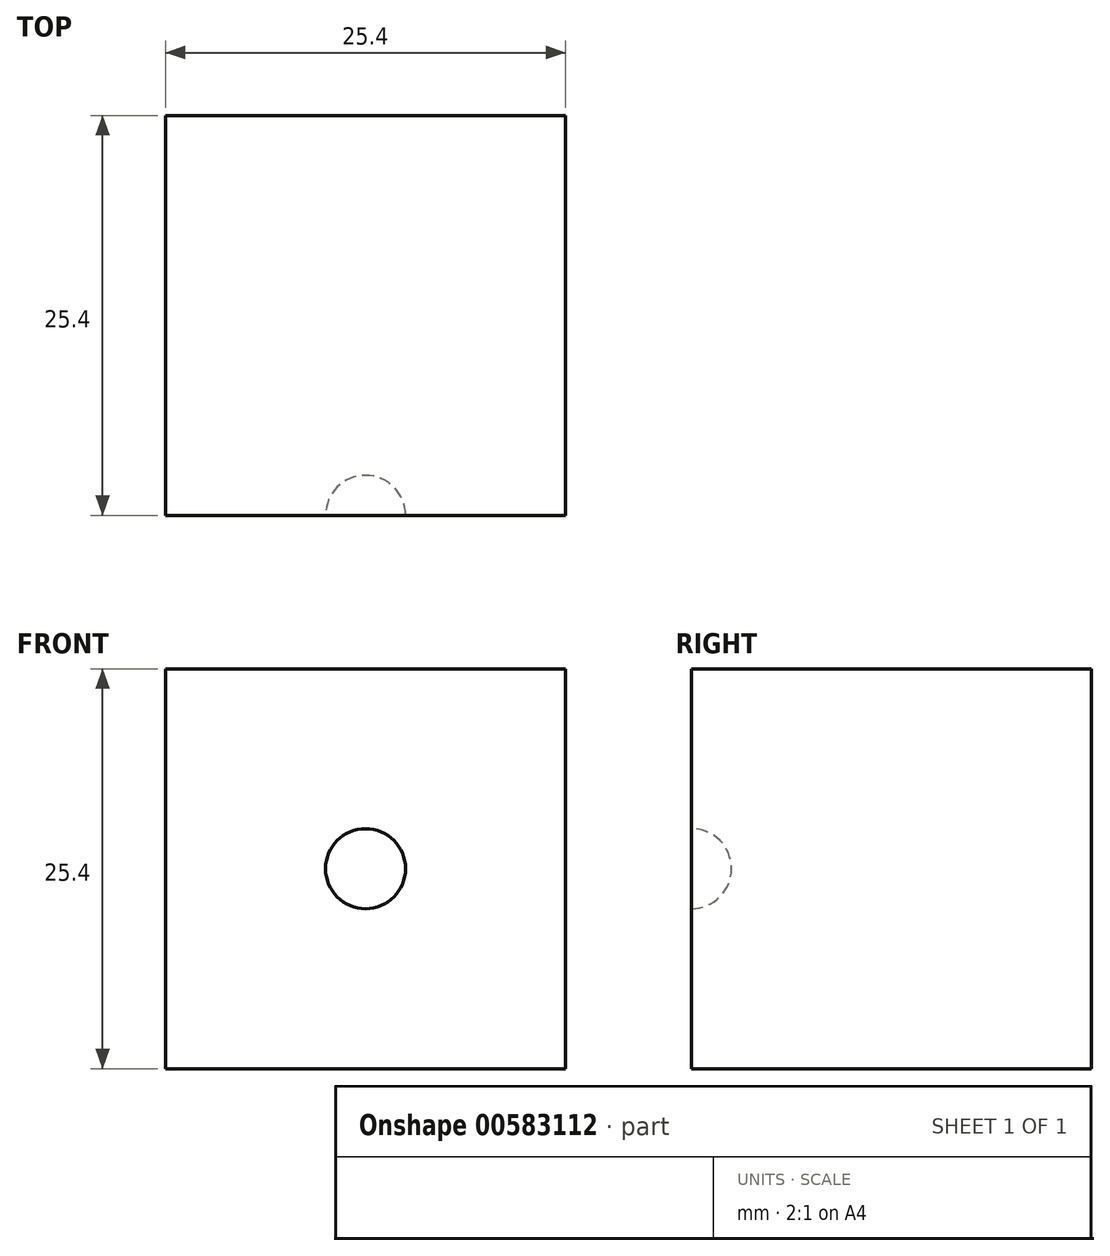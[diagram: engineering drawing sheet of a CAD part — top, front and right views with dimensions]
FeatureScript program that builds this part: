
annotation { "Feature Type Name" : "Feature", "Feature Type Description" : "" }
export const myFeature = defineFeature(function(context is Context, id is Id, definition is map)
    precondition{}
    {
        {
            var Q0;
            Q0=qCreatedBy(makeId("Front.planeOp"),FACE);
            var sketch = newSketch(context, id + "F0", { "sketchPlane" : qUnion([Q0])});
            skLineSegment(sketch, "E0.bottom", {"start": v(0, 0) * mm, "end": v(25.4, 0) * mm});
            skLineSegment(sketch, "E0.top", {"start": v(0, 25.4) * mm, "end": v(25.4, 25.4) * mm});
            skLineSegment(sketch, "E0.left", {"start": v(0, 0) * mm, "end": v(0, 25.4) * mm});
            skLineSegment(sketch, "E0.right", {"start": v(25.4, 0) * mm, "end": v(25.4, 25.4) * mm});
            skSolve(sketch);
        }
        {
            var Q0;
            Q0 = qSketchRegion(id + "F0", true);
            extrude(context, id + "F1", {"entities" : qUnion([Q0]), "depth" : 25.4 * mm, "offsetDistance" : 25.4 * mm});
        }
        {
            var Q0;
            Q0=makeQuery(id+"F1.opExtrude","CAP_FACE",FACE,{"disambiguationData":[OSD([sQuery(id+"F0.wireOp",EDGE,"E0.bottom"),sQuery(id+"F0.wireOp",EDGE,"E0.top"),sQuery(id+"F0.wireOp",EDGE,"E0.left"),sQuery(id+"F0.wireOp",EDGE,"E0.right")])],"isStart":false});
            var sketch = newSketch(context, id + "F2", { "sketchPlane" : qUnion([Q0])});
            skLineSegment(sketch, "E1", {"start": v(12.7, 25.4) * mm, "end": v(12.7, 0) * mm});
            skArc(sketch, "E2", {"start": v(12.7, 10.16) * mm, "mid": v(15.24, 12.7) * mm, "end": v(12.7, 15.24) * mm});
            skSolve(sketch);
        }
        {
            var Q0;
            Q0 = qSketchRegion(id + "F2", true);
            var Q1;
            Q1=sQuery(id+"F2.wireOp",EDGE,"E1");
            revolve(context, id + "F3", {"operationType" : NewBodyOperationType.REMOVE, "entities" : qUnion([Q0]), "axis" : qUnion([Q1]), "revolveType" : RevolveType.FULL, "oppositeDirection" : true});
        }
    });
